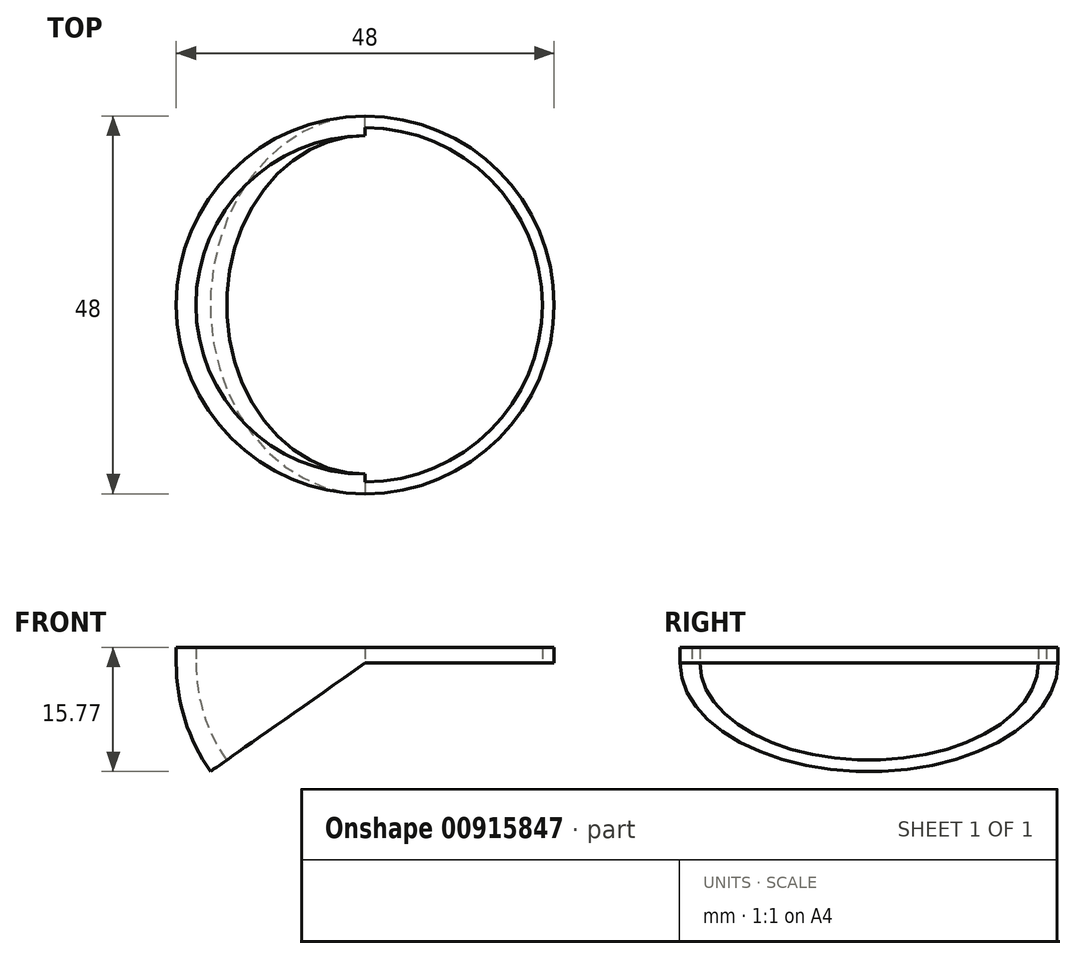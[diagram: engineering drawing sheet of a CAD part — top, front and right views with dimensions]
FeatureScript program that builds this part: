
annotation { "Feature Type Name" : "Feature", "Feature Type Description" : "" }
export const myFeature = defineFeature(function(context is Context, id is Id, definition is map)
    precondition{}
    {
        {
            var Q0;
            Q0=qCreatedBy(makeId("Top.planeOp"),FACE);
            var sketch = newSketch(context, id + "F0", { "sketchPlane" : qUnion([Q0])});
            skCircle(sketch, "E0", {"center": v(0, 0) * mm, "radius": 22.5 * mm});
            skCircle(sketch, "E1", {"center": v(0, 0) * mm, "radius": 24 * mm});
            skSolve(sketch);
        }
        {
            var Q0;
            Q0=makeQuery(id+"F0.imprint","IMPRINT",FACE,{"disambiguationData":[TD([[makeQuery(id+"F0.imprint","IMPRINT",EDGE,{"derivedFrom":sQuery(id+"F0.wireOp",EDGE,"E0")}),-1.0]])]});
            extrude(context, id + "F1", {"entities" : qUnion([Q0]), "depth" : 2 * mm, "offsetDistance" : 25 * mm});
        }
        {
            var Q0;
            Q0=qCreatedBy(makeId("Top.planeOp"),FACE);
            var sketch = newSketch(context, id + "F2", { "sketchPlane" : qUnion([Q0])});
            skLineSegment(sketch, "E2", {"start": v(0, 24) * mm, "end": v(0, -24) * mm, "construction": true});
            skArc(sketch, "E3", {"start": v(0, 24) * mm, "mid": v(-24, 0) * mm, "end": v(0, -24) * mm});
            skArc(sketch, "E4", {"start": v(0, -24) * mm, "mid": v(24, 0) * mm, "end": v(0, 24) * mm});
            skPoint(sketch, "E5", {"position": v(0, 21.5) * mm});
            skPoint(sketch, "E6", {"position": v(0, -21.5) * mm});
            skArc(sketch, "E7", {"start": v(0, 21.5) * mm, "mid": v(-21.5, 0) * mm, "end": v(0, -21.5) * mm});
            skArc(sketch, "E8", {"start": v(0, -21.5) * mm, "mid": v(21.5, 0) * mm, "end": v(0, 21.5) * mm});
            skLineSegment(sketch, "E9", {"start": v(0, 21.5) * mm, "end": v(0, 24) * mm});
            skLineSegment(sketch, "E10", {"start": v(0, -21.5) * mm, "end": v(0, -24) * mm});
            skSolve(sketch);
        }
        {
            var Q0;
            Q0=makeQuery(id+"F2.imprint","IMPRINT",FACE,{"disambiguationData":[TD([[makeQuery(id+"F2.imprint","IMPRINT",EDGE,{"derivedFrom":sQuery(id+"F2.wireOp",EDGE,"E3")}),1.0]])]});
            var Q1;
            Q1=sQuery(id+"F2.wireOp",EDGE,"E2");
            revolve(context, id + "F3", {"operationType" : NewBodyOperationType.ADD, "surfaceOperationType" : NewSurfaceOperationType.NEW, "entities" : qUnion([Q0]), "axis" : qUnion([Q1]), "revolveType" : RevolveType.ONE_DIRECTION, "angle" : 35 * degree});
        }
        {
            var Q0;
            Q0=makeQuery(id+"F2.imprint","IMPRINT",FACE,{"disambiguationData":[TD([[makeQuery(id+"F2.imprint","IMPRINT",EDGE,{"derivedFrom":sQuery(id+"F2.wireOp",EDGE,"E3")}),1.0]])]});
            extrude(context, id + "F4", {"entities" : qUnion([Q0]), "operationType" : NewBodyOperationType.ADD, "depth" : 2 * mm, "offsetDistance" : 25 * mm});
        }
    });
